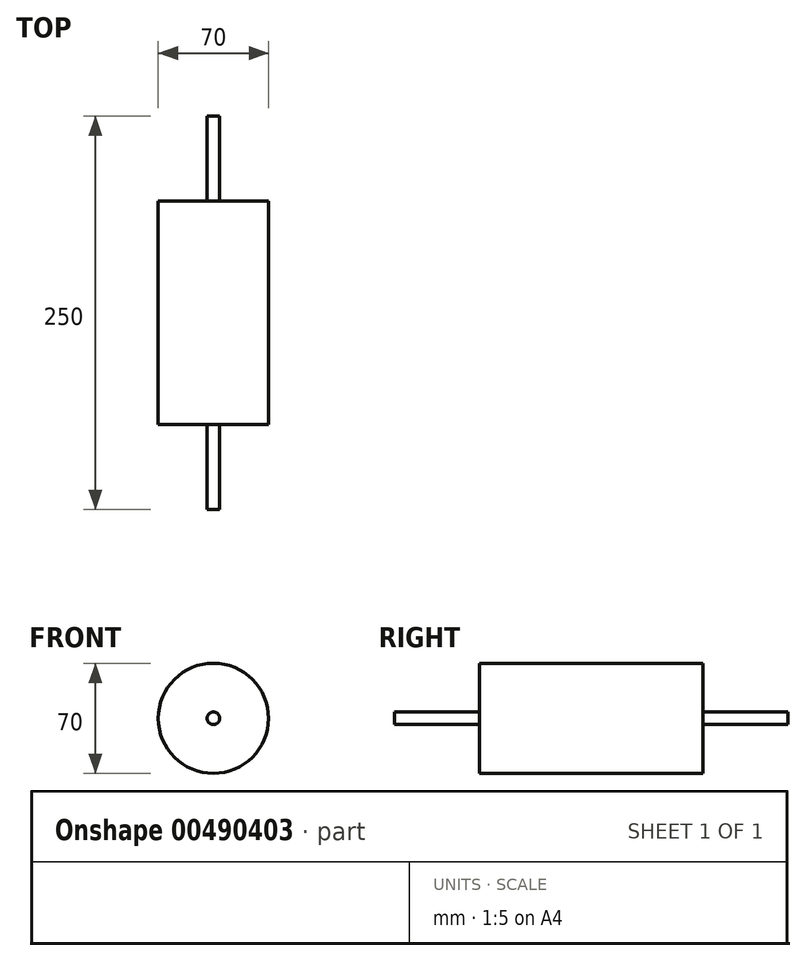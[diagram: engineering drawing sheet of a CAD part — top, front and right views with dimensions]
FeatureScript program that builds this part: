
annotation { "Feature Type Name" : "Feature", "Feature Type Description" : "" }
export const myFeature = defineFeature(function(context is Context, id is Id, definition is map)
    precondition{}
    {
        {
            var Q0;
            Q0=qCreatedBy(makeId("Front.planeOp"),FACE);
            var sketch = newSketch(context, id + "F0", { "sketchPlane" : qUnion([Q0])});
            skCircle(sketch, "E0", {"center": v(0, 0) * mm, "radius": 4 * mm});
            skCircle(sketch, "E1", {"center": v(0, 0) * mm, "radius": 35 * mm});
            skSolve(sketch);
        }
        {
            var Q0;
            Q0=makeQuery(id+"F0.imprint","IMPRINT",FACE,{"disambiguationData":[TD([[makeQuery(id+"F0.imprint","IMPRINT",EDGE,{"derivedFrom":sQuery(id+"F0.wireOp",EDGE,"E0")}),1.0]])]});
            extrude(context, id + "F1", {"entities" : qUnion([Q0]), "depth" : 250 * mm});
        }
        {
            var Q0;
            Q0=makeQuery(id+"F0.imprint","IMPRINT",FACE,{"disambiguationData":[TD([[makeQuery(id+"F0.imprint","IMPRINT",EDGE,{"derivedFrom":sQuery(id+"F0.wireOp",EDGE,"E0")}),-1.0]])]});
            extrude(context, id + "F2", {"entities" : qUnion([Q0]), "operationType" : NewBodyOperationType.ADD, "depth" : 196 * mm, "hasSecondDirection" : true, "secondDirectionOppositeDirection" : false, "secondDirectionDepth" : 54 * mm});
        }
    });
